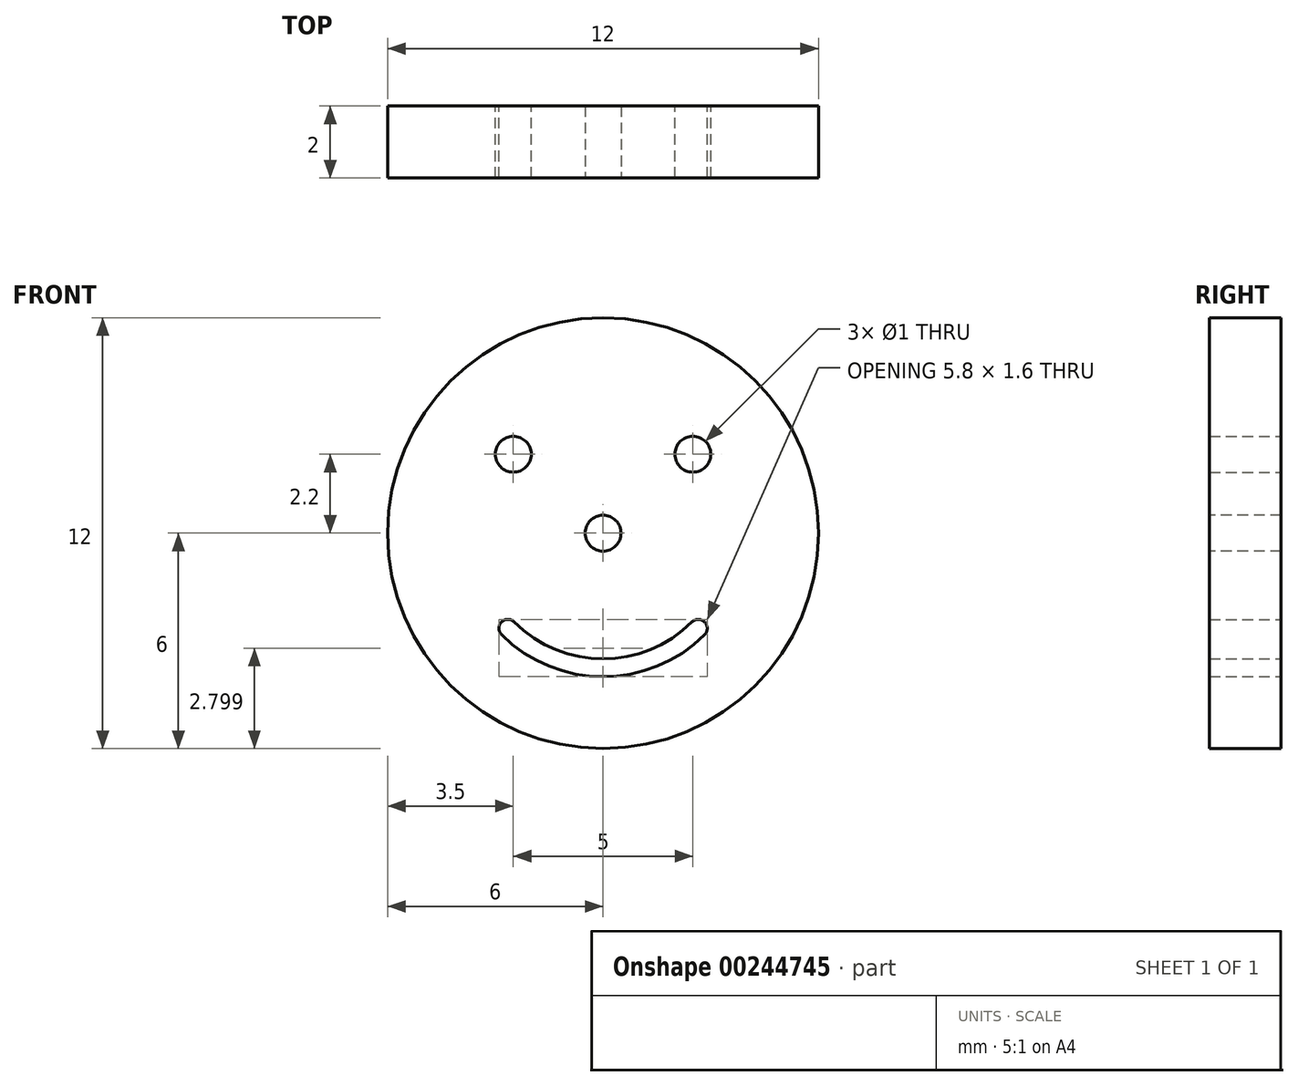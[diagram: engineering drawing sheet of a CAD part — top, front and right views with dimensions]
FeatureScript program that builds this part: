
annotation { "Feature Type Name" : "Feature", "Feature Type Description" : "" }
export const myFeature = defineFeature(function(context is Context, id is Id, definition is map)
    precondition{}
    {
        {
            var Q0;
            Q0=qCreatedBy(makeId("Front.planeOp"),FACE);
            var sketch = newSketch(context, id + "F0", { "sketchPlane" : qUnion([Q0])});
            skCircle(sketch, "E0", {"center": v(0, 0) * mm, "radius": 6 * mm});
            skLineSegment(sketch, "E1", {"start": v(0, 0) * mm, "end": v(-2.83, -2.83) * mm, "construction": true});
            skLineSegment(sketch, "E2", {"start": v(0, 0) * mm, "end": v(0, -4.95) * mm, "construction": true});
            skLineSegment(sketch, "E3", {"start": v(0, 0) * mm, "end": v(2.83, -2.83) * mm, "construction": true});
            skArc(sketch, "E4", {"start": v(2.83, -2.83) * mm, "mid": v(0, -4) * mm, "end": v(-2.83, -2.83) * mm});
            skArc(sketch, "E5", {"start": v(2.47, -2.47) * mm, "mid": v(0, -3.5) * mm, "end": v(-2.47, -2.47) * mm});
            skPoint(sketch, "E5.startSnap0", {"position": v(0, -2.47) * mm});
            skArc(sketch, "E6", {"start": v(-2.83, -2.83) * mm, "mid": v(-2.83, -2.47) * mm, "end": v(-2.47, -2.47) * mm});
            skArc(sketch, "E7", {"start": v(2.47, -2.47) * mm, "mid": v(2.83, -2.47) * mm, "end": v(2.83, -2.83) * mm});
            skCircle(sketch, "E8", {"center": v(-2.5, 2.2) * mm, "radius": 0.5 * mm});
            skCircle(sketch, "E9", {"center": v(2.5, 2.2) * mm, "radius": 0.5 * mm});
            skSolve(sketch);
        }
        {
            var Q0;
            Q0 = qSketchRegion(id + "F0", true);
            extrude(context, id + "F1", {"entities" : qUnion([Q0]), "depth" : 2 * mm});
        }
        {
            var Q0;
            Q0=makeQuery(id+"F1.opExtrude","CAP_FACE",FACE,{"disambiguationData":[OSD([sQuery(id+"F0.wireOp",EDGE,"E0"),sQuery(id+"F0.wireOp",EDGE,"E4"),sQuery(id+"F0.wireOp",EDGE,"E5"),sQuery(id+"F0.wireOp",EDGE,"E6"),sQuery(id+"F0.wireOp",EDGE,"E7"),sQuery(id+"F0.wireOp",EDGE,"E8"),sQuery(id+"F0.wireOp",EDGE,"E9")])],"isStart":false});
            var sketch = newSketch(context, id + "F2", { "sketchPlane" : qUnion([Q0])});
            skCircle(sketch, "E10", {"center": v(0, 0) * mm, "radius": 0.5 * mm});
            skSolve(sketch);
        }
        {
            var Q0;
            Q0 = qSketchRegion(id + "F2", true);
            extrude(context, id + "F3", {"entities" : qUnion([Q0]), "operationType" : NewBodyOperationType.REMOVE, "oppositeDirection" : true, "depth" : 25 * mm});
        }
    });
